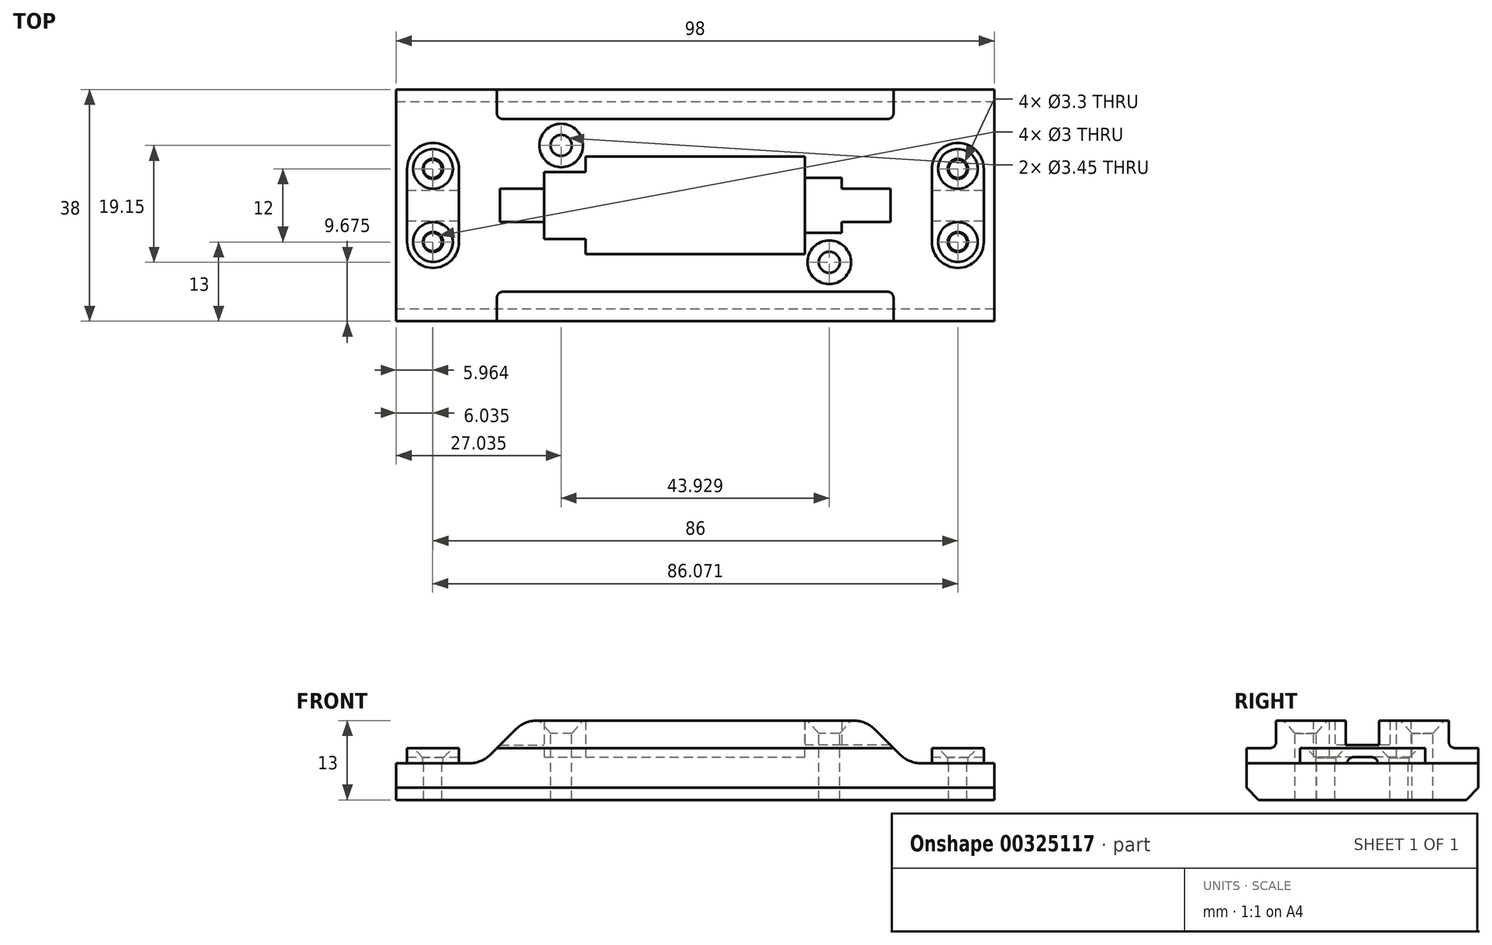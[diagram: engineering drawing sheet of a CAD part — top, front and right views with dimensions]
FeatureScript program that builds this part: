
annotation { "Feature Type Name" : "Feature", "Feature Type Description" : "" }
export const myFeature = defineFeature(function(context is Context, id is Id, definition is map)
    precondition{}
    {
        {
            var Q0;
            Q0=qCreatedBy(makeId("Right.planeOp"),FACE);
            var sketch = newSketch(context, id + "F0", { "sketchPlane" : qUnion([Q0])});
            skLineSegment(sketch, "E0.bottom", {"start": v(19, -4.25) * mm, "end": v(-19, -4.25) * mm});
            skLineSegment(sketch, "E0.top", {"start": v(19, 4.25) * mm, "end": v(14.15, 4.25) * mm});
            skLineSegment(sketch, "E0.left", {"start": v(19, -4.25) * mm, "end": v(19, 4.25) * mm});
            skLineSegment(sketch, "E0.right", {"start": v(-19, -4.25) * mm, "end": v(-19, 4.25) * mm});
            skPoint(sketch, "E0.middle", {"position": v(0, 0) * mm});
            skLineSegment(sketch, "E1.top", {"start": v(14.15, 8.75) * mm, "end": v(-14.15, 8.75) * mm});
            skLineSegment(sketch, "E1.left", {"start": v(14.15, 4.25) * mm, "end": v(14.15, 8.75) * mm});
            skLineSegment(sketch, "E1.right", {"start": v(-14.15, 4.25) * mm, "end": v(-14.15, 8.75) * mm});
            skPoint(sketch, "E1.middle", {"position": v(0, 6.5) * mm});
            skLineSegment(sketch, "E2.trimOffspring", {"start": v(-14.15, 4.25) * mm, "end": v(-19, 4.25) * mm});
            skSolve(sketch);
        }
        {
            var Q0;
            Q0=makeQuery(id+"F0.imprint","IMPRINT",FACE,{"disambiguationData":[TD([[makeQuery(id+"F0.imprint","IMPRINT",EDGE,{"derivedFrom":sQuery(id+"F0.wireOp",EDGE,"E0.bottom")}),-1.0]])]});
            extrude(context, id + "F1", {"entities" : qUnion([Q0]), "depth" : (36 + 10 + 10 + 7 + 7) * mm});
        }
        {
            var Q0;
            Q0=makeQuery(id+"F1.opExtrude","SWEPT_EDGE",EDGE,{"disambiguationData":[OSD([sQuery(id+"F0.wireOp",EDGE,"E0.bottom"),sQuery(id+"F0.wireOp",EDGE,"E0.right")])]});
            var Q1;
            Q1=makeQuery(id+"F1.opExtrude","SWEPT_EDGE",EDGE,{"disambiguationData":[OSD([sQuery(id+"F0.wireOp",EDGE,"E0.bottom"),sQuery(id+"F0.wireOp",EDGE,"E0.left")])]});
            chamfer(context, id + "F2", {"entities" : qUnion([Q0, Q1]), "width" : 2 * mm, "tangentPropagation" : true});
        }
        {
            var Q0;
            Q0=makeQuery(id+"F1.opExtrude","SWEPT_EDGE",EDGE,{"disambiguationData":[OSD([sQuery(id+"F0.wireOp",EDGE,"E0.top"),sQuery(id+"F0.wireOp",EDGE,"E1.left")])]});
            var Q1;
            Q1=makeQuery(id+"F1.opExtrude","SWEPT_EDGE",EDGE,{"disambiguationData":[OSD([sQuery(id+"F0.wireOp",EDGE,"E1.right"),sQuery(id+"F0.wireOp",EDGE,"E2.trimOffspring")])]});
            fillet(context, id + "F3", {"entities" : qUnion([Q0, Q1]), "radius" : 1 * mm, "tangentPropagation" : true, "allowEdgeOverflow" : false});
        }
        {
            var Q0;
            Q0=makeQuery(id+"F1.opExtrude","SWEPT_FACE",FACE,{"disambiguationData":[OSD([sQuery(id+"F0.wireOp",EDGE,"E1.top")])]});
            var sketch = newSketch(context, id + "F4", { "sketchPlane" : qUnion([Q0])});
            skLineSegment(sketch, "E3", {"start": v(0, 0) * mm, "end": v(70, 0) * mm, "construction": true});
            skLineSegment(sketch, "E4.bottom", {"start": v(17, 8) * mm, "end": v(53, 8) * mm});
            skLineSegment(sketch, "E4.top", {"start": v(17, -8) * mm, "end": v(53, -8) * mm});
            skLineSegment(sketch, "E4.left", {"start": v(17, 8) * mm, "end": v(17, -8) * mm});
            skLineSegment(sketch, "E4.right", {"start": v(53, 8) * mm, "end": v(53, -8) * mm});
            skPoint(sketch, "E4.middle", {"position": v(35, 0) * mm});
            skSolve(sketch);
        }
        {
            var Q0;
            Q0=makeQuery(id+"F1.opExtrude","CAP_EDGE",EDGE,{"disambiguationData":[OSD([sQuery(id+"F0.wireOp",EDGE,"E1.top")])],"isStart":false});
            var Q1;
            Q1=makeQuery(id+"F1.opExtrude","CAP_EDGE",EDGE,{"disambiguationData":[OSD([sQuery(id+"F0.wireOp",EDGE,"E1.top")])],"isStart":true});
            chamfer(context, id + "F5", {"entities" : qUnion([Q0, Q1]), "width" : 7 * mm, "tangentPropagation" : true});
        }
        {
            var Q0;
            Q0=makeQuery(id+"F1.opExtrude","CAP_FACE",FACE,{"disambiguationData":[OSD([sQuery(id+"F0.wireOp",EDGE,"E0.bottom"),sQuery(id+"F0.wireOp",EDGE,"E0.top"),sQuery(id+"F0.wireOp",EDGE,"E0.left"),sQuery(id+"F0.wireOp",EDGE,"E0.right"),sQuery(id+"F0.wireOp",EDGE,"E1.top"),sQuery(id+"F0.wireOp",EDGE,"E1.left"),sQuery(id+"F0.wireOp",EDGE,"E1.right"),sQuery(id+"F0.wireOp",EDGE,"E2.trimOffspring")])],"isStart":true});
            extrude(context, id + "F6", {"entities" : qUnion([Q0]), "operationType" : NewBodyOperationType.ADD, "depth" : 14 * mm});
        }
        {
            var Q0;
            Q0=makeQuery(id+"F1.opExtrude","CAP_FACE",FACE,{"disambiguationData":[OSD([sQuery(id+"F0.wireOp",EDGE,"E0.bottom"),sQuery(id+"F0.wireOp",EDGE,"E0.top"),sQuery(id+"F0.wireOp",EDGE,"E0.left"),sQuery(id+"F0.wireOp",EDGE,"E0.right"),sQuery(id+"F0.wireOp",EDGE,"E1.top"),sQuery(id+"F0.wireOp",EDGE,"E1.left"),sQuery(id+"F0.wireOp",EDGE,"E1.right"),sQuery(id+"F0.wireOp",EDGE,"E2.trimOffspring")])],"isStart":false});
            extrude(context, id + "F7", {"entities" : qUnion([Q0]), "operationType" : NewBodyOperationType.ADD, "depth" : 14 * mm});
        }
        {
            var Q0;
            {var subQ0=sQuery(id+"F0.wireOp",EDGE,"E1.top");Q0=makeQuery(id+"F5.opChamfer","BLEND_EDGE",EDGE,{"blendedFrom":[makeQuery(id+"F1.opExtrude","CAP_EDGE",EDGE,{"disambiguationData":[OSD([subQ0])],"isStart":false}),makeQuery(id+"F1.opExtrude","SWEPT_FACE",FACE,{"disambiguationData":[OSD([subQ0])]})],"blendedInto":[makeQuery(id+"F1.opExtrude","SWEPT_FACE",FACE,{"disambiguationData":[OSD([subQ0])]})]});}
            var Q1;
            {var subQ0=sQuery(id+"F0.wireOp",EDGE,"E2.trimOffspring");var subQ1=sQuery(id+"F0.wireOp",EDGE,"E1.right");var subQ2=sQuery(id+"F0.wireOp",EDGE,"E1.left");var subQ3=sQuery(id+"F0.wireOp",EDGE,"E1.top");var subQ4=sQuery(id+"F0.wireOp",EDGE,"E0.right");var subQ5=sQuery(id+"F0.wireOp",EDGE,"E0.left");var subQ6=sQuery(id+"F0.wireOp",EDGE,"E0.top");var subQ7=sQuery(id+"F0.wireOp",EDGE,"E0.bottom");var subQ8=makeQuery(id+"F5.opChamfer","BLEND_EDGE",EDGE,{"blendedFrom":[makeQuery(id+"F1.opExtrude","CAP_EDGE",EDGE,{"disambiguationData":[OSD([subQ3])],"isStart":false}),makeQuery(id+"F1.opExtrude","CAP_FACE",FACE,{"disambiguationData":[OSD([subQ7,subQ6,subQ5,subQ4,subQ3,subQ2,subQ1,subQ0])],"isStart":false})],"blendedInto":[makeQuery(id+"F1.opExtrude","CAP_FACE",FACE,{"disambiguationData":[OSD([subQ7,subQ6,subQ5,subQ4,subQ3,subQ2,subQ1,subQ0])],"isStart":false})]});Q1=makeQuery(id+"F7.boolean.opBoolean","MERGE",EDGE,{"derivedFrom":[subQ8,makeQuery(id+"F7.opExtrude","CAP_EDGE",EDGE,{"disambiguationData":[OSD([subQ7,subQ6,subQ5,subQ4,subQ3,subQ2,subQ1,subQ0]),TDD([subQ8])],"isStart":true})]});}
            var Q2;
            {var subQ0=sQuery(id+"F0.wireOp",EDGE,"E1.top");Q2=makeQuery(id+"F5.opChamfer","BLEND_EDGE",EDGE,{"blendedFrom":[makeQuery(id+"F1.opExtrude","CAP_EDGE",EDGE,{"disambiguationData":[OSD([subQ0])],"isStart":true}),makeQuery(id+"F1.opExtrude","SWEPT_FACE",FACE,{"disambiguationData":[OSD([subQ0])]})],"blendedInto":[makeQuery(id+"F1.opExtrude","SWEPT_FACE",FACE,{"disambiguationData":[OSD([subQ0])]})]});}
            var Q3;
            {var subQ0=sQuery(id+"F0.wireOp",EDGE,"E2.trimOffspring");var subQ1=sQuery(id+"F0.wireOp",EDGE,"E1.right");var subQ2=sQuery(id+"F0.wireOp",EDGE,"E1.left");var subQ3=sQuery(id+"F0.wireOp",EDGE,"E1.top");var subQ4=sQuery(id+"F0.wireOp",EDGE,"E0.right");var subQ5=sQuery(id+"F0.wireOp",EDGE,"E0.left");var subQ6=sQuery(id+"F0.wireOp",EDGE,"E0.top");var subQ7=sQuery(id+"F0.wireOp",EDGE,"E0.bottom");var subQ8=makeQuery(id+"F5.opChamfer","BLEND_EDGE",EDGE,{"blendedFrom":[makeQuery(id+"F1.opExtrude","CAP_EDGE",EDGE,{"disambiguationData":[OSD([subQ3])],"isStart":true}),makeQuery(id+"F1.opExtrude","CAP_FACE",FACE,{"disambiguationData":[OSD([subQ7,subQ6,subQ5,subQ4,subQ3,subQ2,subQ1,subQ0])],"isStart":true})],"blendedInto":[makeQuery(id+"F1.opExtrude","CAP_FACE",FACE,{"disambiguationData":[OSD([subQ7,subQ6,subQ5,subQ4,subQ3,subQ2,subQ1,subQ0])],"isStart":true})]});Q3=makeQuery(id+"F6.boolean.opBoolean","MERGE",EDGE,{"derivedFrom":[subQ8,makeQuery(id+"F6.opExtrude","CAP_EDGE",EDGE,{"disambiguationData":[OSD([subQ7,subQ6,subQ5,subQ4,subQ3,subQ2,subQ1,subQ0]),TDD([subQ8])],"isStart":true})]});}
            fillet(context, id + "F8", {"entities" : qUnion([Q0, Q1, Q2, Q3]), "radius" : 5 * mm, "tangentPropagation" : true, "allowEdgeOverflow" : false});
        }
        {
            var Q0;
            Q0=makeQuery(id+"F4.imprint","IMPRINT",FACE,{"disambiguationData":[TD([[makeQuery(id+"F4.imprint","IMPRINT",EDGE,{"derivedFrom":sQuery(id+"F4.wireOp",EDGE,"E4.bottom")}),-1.0]])]});
            extrude(context, id + "F9", {"entities" : qUnion([Q0]), "operationType" : NewBodyOperationType.REMOVE, "oppositeDirection" : true, "depth" : 6 * mm});
        }
        {
            var Q0;
            Q0=makeQuery(id+"F9.boolean.opBoolean","COPY",FACE,{"derivedFrom":makeQuery(id+"F9.opExtrude","SWEPT_FACE",FACE,{"disambiguationData":[OSD([sQuery(id+"F4.wireOp",EDGE,"E4.left")])]})});
            var sketch = newSketch(context, id + "F10", { "sketchPlane" : qUnion([Q0])});
            skLineSegment(sketch, "E5", {"start": v(0, 8.75) * mm, "end": v(0, 2.75) * mm, "construction": true});
            skLineSegment(sketch, "E6.bottom", {"start": v(5.5, 8.75) * mm, "end": v(-5.5, 8.75) * mm});
            skLineSegment(sketch, "E6.top", {"start": v(5.5, 2.75) * mm, "end": v(-5.5, 2.75) * mm});
            skLineSegment(sketch, "E6.left", {"start": v(5.5, 8.75) * mm, "end": v(5.5, 2.75) * mm});
            skLineSegment(sketch, "E6.right", {"start": v(-5.5, 8.75) * mm, "end": v(-5.5, 2.75) * mm});
            skPoint(sketch, "E6.middle", {"position": v(0, 5.75) * mm});
            skSolve(sketch);
        }
        {
            var Q0;
            Q0=makeQuery(id+"F10.imprint","IMPRINT",FACE,{"disambiguationData":[TD([[makeQuery(id+"F10.imprint","IMPRINT",EDGE,{"derivedFrom":sQuery(id+"F10.wireOp",EDGE,"E6.bottom")}),1.0]])]});
            extrude(context, id + "F11", {"entities" : qUnion([Q0]), "operationType" : NewBodyOperationType.REMOVE, "oppositeDirection" : true, "depth" : 6.75 * mm});
        }
        {
            var Q0;
            Q0=makeQuery(id+"F9.boolean.opBoolean","COPY",FACE,{"derivedFrom":makeQuery(id+"F9.opExtrude","SWEPT_FACE",FACE,{"disambiguationData":[OSD([sQuery(id+"F4.wireOp",EDGE,"E4.right")])]})});
            var sketch = newSketch(context, id + "F12", { "sketchPlane" : qUnion([Q0])});
            skLineSegment(sketch, "E7", {"start": v(-8, 5.75) * mm, "end": v(8, 5.75) * mm, "construction": true});
            skLineSegment(sketch, "E8.bottom", {"start": v(-4.5, 8.75) * mm, "end": v(4.5, 8.75) * mm});
            skLineSegment(sketch, "E8.top", {"start": v(-4.5, 4.75) * mm, "end": v(4.5, 4.75) * mm});
            skLineSegment(sketch, "E8.left", {"start": v(-4.5, 8.75) * mm, "end": v(-4.5, 4.75) * mm});
            skLineSegment(sketch, "E8.right", {"start": v(4.5, 8.75) * mm, "end": v(4.5, 4.75) * mm});
            skPoint(sketch, "E8.middle", {"position": v(0, 6.75) * mm});
            skPoint(sketch, "E8.middle.positionSnap0", {"position": v(0, 5.75) * mm});
            skPoint(sketch, "E8.centerSnap0", {"position": v(0, 5.75) * mm});
            skSolve(sketch);
        }
        {
            var Q0;
            Q0=makeQuery(id+"F12.imprint","IMPRINT",FACE,{"disambiguationData":[TD([[makeQuery(id+"F12.imprint","IMPRINT",EDGE,{"derivedFrom":sQuery(id+"F12.wireOp",EDGE,"E8.bottom")}),-1.0]])]});
            extrude(context, id + "F13", {"entities" : qUnion([Q0]), "operationType" : NewBodyOperationType.REMOVE, "oppositeDirection" : true, "depth" : 6 * mm});
        }
        {
            var Q0;
            Q0=makeQuery(id+"F13.boolean.opBoolean","COPY",FACE,{"derivedFrom":makeQuery(id+"F13.opExtrude","CAP_FACE",FACE,{"disambiguationData":[OSD([sQuery(id+"F12.wireOp",EDGE,"E8.bottom"),sQuery(id+"F12.wireOp",EDGE,"E8.top"),sQuery(id+"F12.wireOp",EDGE,"E8.left"),sQuery(id+"F12.wireOp",EDGE,"E8.right")])],"isStart":false})});
            var sketch = newSketch(context, id + "F14", { "sketchPlane" : qUnion([Q0])});
            skLineSegment(sketch, "E9", {"start": v(4.5, 6.75) * mm, "end": v(-4.5, 6.75) * mm, "construction": true});
            skLineSegment(sketch, "E10.bottom", {"start": v(-2.75, 8.75) * mm, "end": v(2.75, 8.75) * mm});
            skLineSegment(sketch, "E10.top", {"start": v(-2.75, 4.75) * mm, "end": v(2.75, 4.75) * mm});
            skLineSegment(sketch, "E10.left", {"start": v(-2.75, 8.75) * mm, "end": v(-2.75, 4.75) * mm});
            skLineSegment(sketch, "E10.right", {"start": v(2.75, 8.75) * mm, "end": v(2.75, 4.75) * mm});
            skPoint(sketch, "E10.middle", {"position": v(0, 6.75) * mm});
            skPoint(sketch, "E10.middle.positionSnap0", {"position": v(0, 6.75) * mm});
            skPoint(sketch, "E10.centerSnap0", {"position": v(0, 6.75) * mm});
            skSolve(sketch);
        }
        {
            var Q0;
            {var subQ0=sQuery(id+"F14.wireOp",EDGE,"E10.bottom");Q0=makeQuery(id+"F14.imprint","IMPRINT",FACE,{"disambiguationData":[TD([[makeQuery(id+"F14.imprint","IMPRINT",EDGE,{"derivedFrom":subQ0}),-1.0]])]});}
            extrude(context, id + "F15", {"entities" : qUnion([Q0]), "operationType" : NewBodyOperationType.REMOVE, "endBound" : BoundingType.UP_TO_NEXT, "oppositeDirection" : true, "depth" : 25 * mm});
        }
        {
            var Q0;
            {var subQ0=sQuery(id+"F0.wireOp",EDGE,"E2.trimOffspring");var subQ1=sQuery(id+"F0.wireOp",EDGE,"E1.right");var subQ2=sQuery(id+"F0.wireOp",EDGE,"E1.left");var subQ3=sQuery(id+"F0.wireOp",EDGE,"E1.top");var subQ4=sQuery(id+"F0.wireOp",EDGE,"E0.right");var subQ5=sQuery(id+"F0.wireOp",EDGE,"E0.left");var subQ6=sQuery(id+"F0.wireOp",EDGE,"E0.top");var subQ7=sQuery(id+"F0.wireOp",EDGE,"E0.bottom");Q0=makeQuery(id+"F7.opExtrude","SWEPT_FACE",FACE,{"disambiguationData":[OSD([subQ7,subQ6,subQ5,subQ4,subQ3,subQ2,subQ1,subQ0]),TDD([makeQuery(id+"F5.opChamfer","BLEND_EDGE",EDGE,{"blendedFrom":[makeQuery(id+"F1.opExtrude","CAP_EDGE",EDGE,{"disambiguationData":[OSD([subQ3])],"isStart":false}),makeQuery(id+"F1.opExtrude","CAP_FACE",FACE,{"disambiguationData":[OSD([subQ7,subQ6,subQ5,subQ4,subQ3,subQ2,subQ1,subQ0])],"isStart":false})],"blendedInto":[makeQuery(id+"F1.opExtrude","CAP_FACE",FACE,{"disambiguationData":[OSD([subQ7,subQ6,subQ5,subQ4,subQ3,subQ2,subQ1,subQ0])],"isStart":false})]})])]});}
            var sketch = newSketch(context, id + "F16", { "sketchPlane" : qUnion([Q0])});
            skLineSegment(sketch, "E11", {"start": v(78.04, -19) * mm, "end": v(78.04, 19) * mm, "construction": true});
            skPoint(sketch, "E12", {"position": v(78.04, -6) * mm});
            skPoint(sketch, "E13", {"position": v(78.04, 6) * mm});
            skSolve(sketch);
        }
        {
            var Q0;
            Q0=makeQuery(id+"F11.boolean.opBoolean","COPY",FACE,{"derivedFrom":makeQuery(id+"F11.opExtrude","CAP_FACE",FACE,{"disambiguationData":[OSD([sQuery(id+"F10.wireOp",EDGE,"E6.bottom"),sQuery(id+"F10.wireOp",EDGE,"E6.top"),sQuery(id+"F10.wireOp",EDGE,"E6.left"),sQuery(id+"F10.wireOp",EDGE,"E6.right")])],"isStart":false})});
            var sketch = newSketch(context, id + "F17", { "sketchPlane" : qUnion([Q0])});
            skLineSegment(sketch, "E14.0", {"start": v(-2.75, 8.75) * mm, "end": v(-2.75, 4.75) * mm});
            skLineSegment(sketch, "E15.0", {"start": v(2.75, 8.75) * mm, "end": v(2.75, 4.75) * mm});
            skLineSegment(sketch, "E16.0", {"start": v(2.75, 4.75) * mm, "end": v(-2.75, 4.75) * mm});
            skSolve(sketch);
        }
        {
            var Q0;
            {var subQ0=sQuery(id+"F17.wireOp",EDGE,"E14.0");Q0=makeQuery(id+"F17.imprint","IMPRINT",FACE,{"disambiguationData":[TD([[makeQuery(id+"F17.imprint","IMPRINT",EDGE,{"derivedFrom":subQ0}),1.0]])]});}
            extrude(context, id + "F18", {"entities" : qUnion([Q0]), "operationType" : NewBodyOperationType.REMOVE, "endBound" : BoundingType.UP_TO_NEXT, "oppositeDirection" : true, "depth" : 25 * mm});
        }
        {
            var Q0;
            {var subQ0=sQuery(id+"F0.wireOp",EDGE,"E2.trimOffspring");var subQ1=sQuery(id+"F0.wireOp",EDGE,"E1.right");var subQ2=sQuery(id+"F0.wireOp",EDGE,"E1.left");var subQ3=sQuery(id+"F0.wireOp",EDGE,"E1.top");var subQ4=sQuery(id+"F0.wireOp",EDGE,"E0.right");var subQ5=sQuery(id+"F0.wireOp",EDGE,"E0.left");var subQ6=sQuery(id+"F0.wireOp",EDGE,"E0.top");var subQ7=sQuery(id+"F0.wireOp",EDGE,"E0.bottom");Q0=makeQuery(id+"F6.opExtrude","SWEPT_FACE",FACE,{"disambiguationData":[OSD([subQ7,subQ6,subQ5,subQ4,subQ3,subQ2,subQ1,subQ0]),TDD([makeQuery(id+"F5.opChamfer","BLEND_EDGE",EDGE,{"blendedFrom":[makeQuery(id+"F1.opExtrude","CAP_EDGE",EDGE,{"disambiguationData":[OSD([subQ3])],"isStart":true}),makeQuery(id+"F1.opExtrude","CAP_FACE",FACE,{"disambiguationData":[OSD([subQ7,subQ6,subQ5,subQ4,subQ3,subQ2,subQ1,subQ0])],"isStart":true})],"blendedInto":[makeQuery(id+"F1.opExtrude","CAP_FACE",FACE,{"disambiguationData":[OSD([subQ7,subQ6,subQ5,subQ4,subQ3,subQ2,subQ1,subQ0])],"isStart":true})]})])]});}
            var sketch = newSketch(context, id + "F19", { "sketchPlane" : qUnion([Q0])});
            skLineSegment(sketch, "E17", {"start": v(-8.04, -19) * mm, "end": v(-8.04, 19) * mm, "construction": true});
            skPoint(sketch, "E18", {"position": v(-8.04, -6) * mm});
            skPoint(sketch, "E19", {"position": v(-8.04, 6) * mm});
            skSolve(sketch);
        }
        {
            var Q0;
            Q0=sQuery(id+"F16.wireOp",VERTEX,"E12");
            var Q1;
            Q1=sQuery(id+"F16.wireOp",VERTEX,"E13");
            var Q2;
            Q2=sQuery(id+"F19.wireOp",VERTEX,"E19");
            var Q3;
            Q3=sQuery(id+"F19.wireOp",VERTEX,"E18");
            var Q4;
            Q4=makeQuery(id+"F1.opExtrude","SWEPT_BODY",BODY,{"disambiguationData":[OSD([sQuery(id+"F0.wireOp",EDGE,"E0.bottom"),sQuery(id+"F0.wireOp",EDGE,"E0.top"),sQuery(id+"F0.wireOp",EDGE,"E0.left"),sQuery(id+"F0.wireOp",EDGE,"E0.right"),sQuery(id+"F0.wireOp",EDGE,"E1.top"),sQuery(id+"F0.wireOp",EDGE,"E1.left"),sQuery(id+"F0.wireOp",EDGE,"E1.right"),sQuery(id+"F0.wireOp",EDGE,"E2.trimOffspring")])]});
            hole(context, id + "F20", {"style" : HoleStyle.SIMPLE, "endStyle" : HoleEndStyle.BLIND, "standardTappedOrClearance" : lookupTablePath({ "standard" : "ISO", "size" : "3", "type" : "Drilled" }), "standardBlindInLast" : lookupTablePath({ "standard" : "ISO", "size" : "3", "type" : "Drilled" }), "holeDiameter" : 3 * mm, "holeDepth" : 13.8 * mm, "tappedDepth" : 12 * mm, "tapClearance" : 3, "startFromSketch" : true, "locations" : qUnion([Q0, Q1, Q2, Q3]), "scope" : qUnion([Q4])});
        }
        {
            var Q0;
            {var subQ2=sQuery(id+"F0.wireOp",EDGE,"E1.top");var subQ3=makeQuery(id+"F1.opExtrude","SWEPT_FACE",FACE,{"disambiguationData":[OSD([subQ2])]});Q0=makeQuery(id+"F18.boolean.opBoolean","SPLIT",FACE,{"disambiguationData":[TD([makeQuery(id+"F1.opExtrude","SWEPT_FACE",FACE,{"disambiguationData":[OSD([sQuery(id+"F0.wireOp",EDGE,"E1.right")])]})])],"derivedFrom":subQ3});}
            var sketch = newSketch(context, id + "F21", { "sketchPlane" : qUnion([Q0])});
            skLineSegment(sketch, "E20", {"start": v(53, -6.25) * mm, "end": v(60.93, -6.25) * mm, "construction": true});
            skLineSegment(sketch, "E21", {"start": v(56.96, -4.5) * mm, "end": v(56.96, -14.15) * mm, "construction": true});
            skPoint(sketch, "E21.startSnap0", {"position": v(56.96, -6.25) * mm});
            skPoint(sketch, "E22", {"position": v(56.96, -9.32) * mm});
            skSolve(sketch);
        }
        {
            var Q0;
            {var subQ1=sQuery(id+"F0.wireOp",EDGE,"E1.top");var subQ2=makeQuery(id+"F1.opExtrude","SWEPT_FACE",FACE,{"disambiguationData":[OSD([subQ1])]});Q0=makeQuery(id+"F18.boolean.opBoolean","SPLIT",FACE,{"disambiguationData":[TD([makeQuery(id+"F1.opExtrude","SWEPT_FACE",FACE,{"disambiguationData":[OSD([sQuery(id+"F0.wireOp",EDGE,"E1.left")])]})])],"derivedFrom":subQ2});}
            var sketch = newSketch(context, id + "F22", { "sketchPlane" : qUnion([Q0])});
            skLineSegment(sketch, "E23", {"start": v(17, 6.75) * mm, "end": v(9.07, 6.75) * mm, "construction": true});
            skPoint(sketch, "E23.endSnap0", {"position": v(9.07, 8.45) * mm});
            skLineSegment(sketch, "E24", {"start": v(13.04, 5.5) * mm, "end": v(13.04, 14.15) * mm, "construction": true});
            skPoint(sketch, "E24.startSnap0", {"position": v(13.04, 6.75) * mm});
            skPoint(sketch, "E25", {"position": v(13.04, 9.83) * mm});
            skSolve(sketch);
        }
        {
            var Q0;
            Q0=sQuery(id+"F21.wireOp",VERTEX,"E22");
            var Q1;
            Q1=sQuery(id+"F22.wireOp",VERTEX,"E25");
            var Q2;
            Q2=makeQuery(id+"F1.opExtrude","SWEPT_BODY",BODY,{"disambiguationData":[OSD([sQuery(id+"F0.wireOp",EDGE,"E0.bottom"),sQuery(id+"F0.wireOp",EDGE,"E0.top"),sQuery(id+"F0.wireOp",EDGE,"E0.left"),sQuery(id+"F0.wireOp",EDGE,"E0.right"),sQuery(id+"F0.wireOp",EDGE,"E1.top"),sQuery(id+"F0.wireOp",EDGE,"E1.left"),sQuery(id+"F0.wireOp",EDGE,"E1.right"),sQuery(id+"F0.wireOp",EDGE,"E2.trimOffspring")])]});
            hole(context, id + "F23", {"style" : HoleStyle.C_SINK, "endStyle" : HoleEndStyle.BLIND, "standardTappedOrClearance" : lookupTablePath({ "standard" : "ANSI", "fit" : "Normal (ASME)", "size" : "#5", "type" : "Clearance" }), "standardBlindInLast" : lookupTablePath({ "fit" : "Free", "standard" : "ANSI", "size" : "#5", "type" : "Clearance" }), "holeDiameter" : 3.45 * mm, "cSinkDiameter" : 7.14 * mm, "cSinkAngle" : 82 * degree, "holeDepth" : 14.4 * mm, "tappedDepth" : 12 * mm, "tapClearance" : 3, "startFromSketch" : true, "locations" : qUnion([Q0, Q1]), "scope" : qUnion([Q2])});
        }
        {
            var Q0;
            {var subQ0=sQuery(id+"F0.wireOp",EDGE,"E2.trimOffspring");var subQ1=sQuery(id+"F0.wireOp",EDGE,"E1.right");var subQ2=sQuery(id+"F0.wireOp",EDGE,"E1.left");var subQ3=sQuery(id+"F0.wireOp",EDGE,"E1.top");var subQ4=sQuery(id+"F0.wireOp",EDGE,"E0.right");var subQ5=sQuery(id+"F0.wireOp",EDGE,"E0.left");var subQ6=sQuery(id+"F0.wireOp",EDGE,"E0.top");var subQ7=sQuery(id+"F0.wireOp",EDGE,"E0.bottom");var subQ8=makeQuery(id+"F1.opExtrude","CAP_FACE",FACE,{"disambiguationData":[OSD([subQ7,subQ6,subQ5,subQ4,subQ3,subQ2,subQ1,subQ0])],"isStart":false});var subQ9=makeQuery(id+"F1.opExtrude","CAP_EDGE",EDGE,{"disambiguationData":[OSD([subQ3])],"isStart":false});var subQ10=makeQuery(id+"F5.opChamfer","BLEND_EDGE",EDGE,{"blendedFrom":[subQ9,subQ8],"blendedInto":[subQ8]});Q0=makeQuery(id+"F16.imprint","IMPRINT",FACE,{"disambiguationData":[TD([[makeQuery(id+"F16.imprint","IMPRINT",EDGE,{"derivedFrom":makeQuery(id+"F7.opExtrude","CAP_EDGE",EDGE,{"disambiguationData":[OSD([subQ7,subQ6,subQ5,subQ4,subQ3,subQ2,subQ1,subQ0]),TDD([subQ10])],"isStart":false})}),-1.0]])]});}
            var sketch = newSketch(context, id + "F24", { "sketchPlane" : qUnion([Q0])});
            skPoint(sketch, "E26.0", {"position": v(78.04, -6) * mm});
            skPoint(sketch, "E27.0", {"position": v(78.04, 6) * mm});
            skArc(sketch, "E28", {"start": v(73.79, -6) * mm, "mid": v(78.04, -10.25) * mm, "end": v(82.29, -6) * mm});
            skArc(sketch, "E29", {"start": v(82.29, 6) * mm, "mid": v(78.04, 10.25) * mm, "end": v(73.79, 6) * mm});
            skLineSegment(sketch, "E30", {"start": v(82.29, -6) * mm, "end": v(82.29, 6) * mm});
            skLineSegment(sketch, "E31", {"start": v(73.79, -6) * mm, "end": v(73.79, 6) * mm});
            skSolve(sketch);
        }
        {
            var Q0;
            Q0=makeQuery(id+"F24.imprint","IMPRINT",FACE,{"disambiguationData":[TD([[makeQuery(id+"F24.imprint","IMPRINT",EDGE,{"derivedFrom":sQuery(id+"F24.wireOp",EDGE,"E28")}),1.0]])]});
            extrude(context, id + "F25", {"entities" : qUnion([Q0]), "depth" : 2.5 * mm});
        }
        {
            var Q0;
            Q0=makeQuery(id+"F25.opExtrude","CAP_FACE",FACE,{"disambiguationData":[OSD([sQuery(id+"F24.wireOp",EDGE,"E28"),sQuery(id+"F24.wireOp",EDGE,"E29"),sQuery(id+"F24.wireOp",EDGE,"E30"),sQuery(id+"F24.wireOp",EDGE,"E31")])],"isStart":false});
            var sketch = newSketch(context, id + "F26", { "sketchPlane" : qUnion([Q0])});
            skPoint(sketch, "E32.0", {"position": v(78.04, -6) * mm});
            skPoint(sketch, "E33.0", {"position": v(78.04, 6) * mm});
            skSolve(sketch);
        }
        {
            var Q0;
            {var subQ0=sQuery(id+"F0.wireOp",EDGE,"E2.trimOffspring");var subQ1=sQuery(id+"F0.wireOp",EDGE,"E1.right");var subQ2=sQuery(id+"F0.wireOp",EDGE,"E1.left");var subQ3=sQuery(id+"F0.wireOp",EDGE,"E1.top");var subQ4=sQuery(id+"F0.wireOp",EDGE,"E0.right");var subQ5=sQuery(id+"F0.wireOp",EDGE,"E0.left");var subQ6=sQuery(id+"F0.wireOp",EDGE,"E0.top");var subQ7=sQuery(id+"F0.wireOp",EDGE,"E0.bottom");var subQ8=makeQuery(id+"F1.opExtrude","CAP_FACE",FACE,{"disambiguationData":[OSD([subQ7,subQ6,subQ5,subQ4,subQ3,subQ2,subQ1,subQ0])],"isStart":false});var subQ9=makeQuery(id+"F1.opExtrude","CAP_EDGE",EDGE,{"disambiguationData":[OSD([subQ3])],"isStart":false});var subQ10=makeQuery(id+"F5.opChamfer","BLEND_EDGE",EDGE,{"blendedFrom":[subQ9,subQ8],"blendedInto":[subQ8]});Q0=makeQuery(id+"F16.imprint","IMPRINT",FACE,{"disambiguationData":[TD([[makeQuery(id+"F16.imprint","IMPRINT",EDGE,{"derivedFrom":makeQuery(id+"F7.opExtrude","CAP_EDGE",EDGE,{"disambiguationData":[OSD([subQ7,subQ6,subQ5,subQ4,subQ3,subQ2,subQ1,subQ0]),TDD([subQ10])],"isStart":false})}),-1.0]])]});}
            var sketch = newSketch(context, id + "F27", { "sketchPlane" : qUnion([Q0])});
            skPoint(sketch, "E34.0", {"position": v(78.04, 6) * mm});
            skPoint(sketch, "E35.0", {"position": v(78.04, -6) * mm});
            skLineSegment(sketch, "E36", {"start": v(78.04, 6) * mm, "end": v(78.04, -6) * mm, "construction": true});
            skLineSegment(sketch, "E37.0", {"start": v(73.79, -6) * mm, "end": v(73.79, 6) * mm, "construction": true});
            skLineSegment(sketch, "E38.0", {"start": v(82.29, -6) * mm, "end": v(82.29, 6) * mm, "construction": true});
            skLineSegment(sketch, "E39.bottom", {"start": v(73.79, -2.5) * mm, "end": v(82.29, -2.5) * mm});
            skLineSegment(sketch, "E39.top", {"start": v(73.79, 2.5) * mm, "end": v(82.29, 2.5) * mm});
            skLineSegment(sketch, "E39.left", {"start": v(73.79, -2.5) * mm, "end": v(73.79, 2.5) * mm});
            skLineSegment(sketch, "E39.right", {"start": v(82.29, -2.5) * mm, "end": v(82.29, 2.5) * mm});
            skPoint(sketch, "E39.middle", {"position": v(78.04, 0) * mm});
            skSolve(sketch);
        }
        {
            var Q0;
            Q0=makeQuery(id+"F27.imprint","IMPRINT",FACE,{"disambiguationData":[TD([[makeQuery(id+"F27.imprint","IMPRINT",EDGE,{"derivedFrom":sQuery(id+"F27.wireOp",EDGE,"E39.bottom")}),1.0]])]});
            extrude(context, id + "F28", {"entities" : qUnion([Q0]), "operationType" : NewBodyOperationType.REMOVE, "depth" : 1 * mm});
        }
        {
            var Q0;
            Q0=makeQuery(id+"F28.boolean.opBoolean","COPY",EDGE,{"derivedFrom":makeQuery(id+"F28.opExtrude","CAP_EDGE",EDGE,{"disambiguationData":[OSD([sQuery(id+"F27.wireOp",EDGE,"E39.top")])],"isStart":false})});
            var Q1;
            Q1=makeQuery(id+"F28.boolean.opBoolean","COPY",EDGE,{"derivedFrom":makeQuery(id+"F28.opExtrude","CAP_EDGE",EDGE,{"disambiguationData":[OSD([sQuery(id+"F27.wireOp",EDGE,"E39.bottom")])],"isStart":false})});
            fillet(context, id + "F29", {"entities" : qUnion([Q0, Q1]), "radius" : 1 * mm, "tangentPropagation" : true, "allowEdgeOverflow" : false});
        }
        {
            var Q0;
            Q0=sQuery(id+"F26.wireOp",VERTEX,"E32.0");
            var Q1;
            Q1=sQuery(id+"F26.wireOp",VERTEX,"E33.0");
            var Q2;
            Q2=makeQuery(id+"F25.opExtrude","SWEPT_BODY",BODY,{"disambiguationData":[OSD([sQuery(id+"F24.wireOp",EDGE,"E28"),sQuery(id+"F24.wireOp",EDGE,"E29"),sQuery(id+"F24.wireOp",EDGE,"E30"),sQuery(id+"F24.wireOp",EDGE,"E31")])]});
            hole(context, id + "F30", {"style" : HoleStyle.C_SINK, "endStyle" : HoleEndStyle.BLIND, "holeDiameter" : 3.3 * mm, "cSinkDiameter" : 6.5 * mm, "cSinkAngle" : 90 * degree, "holeDepth" : 14.4 * mm, "tappedDepth" : 12 * mm, "tapClearance" : 3, "startFromSketch" : true, "locations" : qUnion([Q0, Q1]), "scope" : qUnion([Q2])});
        }
        {
            var Q0;
            Q0=makeQuery(id+"F25.opExtrude","SWEPT_BODY",BODY,{"disambiguationData":[OSD([sQuery(id+"F24.wireOp",EDGE,"E28"),sQuery(id+"F24.wireOp",EDGE,"E29"),sQuery(id+"F24.wireOp",EDGE,"E30"),sQuery(id+"F24.wireOp",EDGE,"E31")])]});
            transform(context, id + "F31", {"entities" : qUnion([Q0]), "transformType" : TransformType.TRANSLATION_3D, "dx" : -86 * mm, "dy" : 0 * mm, "dz" : 0 * mm, "makeCopy" : true});
        }
    });
